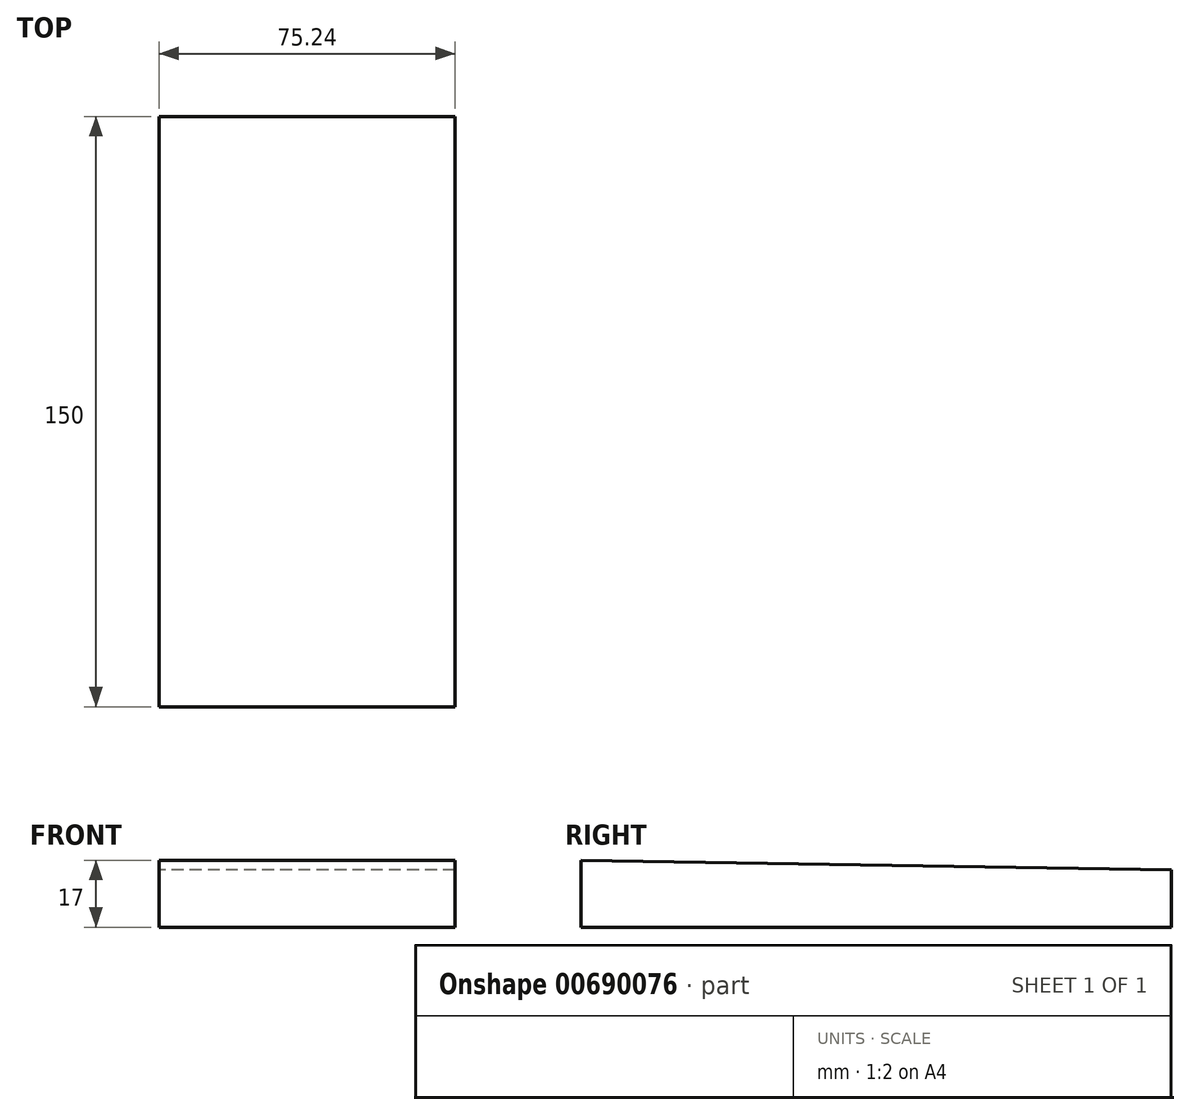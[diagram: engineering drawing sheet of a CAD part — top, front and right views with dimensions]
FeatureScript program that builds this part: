
annotation { "Feature Type Name" : "Feature", "Feature Type Description" : "" }
export const myFeature = defineFeature(function(context is Context, id is Id, definition is map)
    precondition{}
    {
        {
            var Q0;
            Q0=qCreatedBy(makeId("Front.planeOp"),FACE);
            var sketch = newSketch(context, id + "F0", { "sketchPlane" : qUnion([Q0])});
            skLineSegment(sketch, "E0.bottom", {"start": v(37.62, -8) * mm, "end": v(-37.62, -8) * mm});
            skLineSegment(sketch, "E0.top", {"start": v(37.62, 8) * mm, "end": v(-37.62, 8) * mm});
            skLineSegment(sketch, "E0.left", {"start": v(37.62, -8) * mm, "end": v(37.62, 8) * mm});
            skLineSegment(sketch, "E0.right", {"start": v(-37.62, -8) * mm, "end": v(-37.62, 8) * mm});
            skPoint(sketch, "E0.middle", {"position": v(0, 0) * mm});
            skSolve(sketch);
        }
        {
            var Q0;
            Q0=qCreatedBy(makeId("Right.planeOp"),FACE);
            var sketch = newSketch(context, id + "F1", { "sketchPlane" : qUnion([Q0])});
            skLineSegment(sketch, "E1.bottom", {"start": v(0, 8.5) * mm, "end": v(150, 6) * mm});
            skLineSegment(sketch, "E1.top", {"start": v(0, -8.5) * mm, "end": v(150, -8.5) * mm});
            skLineSegment(sketch, "E1.left", {"start": v(0, 8.5) * mm, "end": v(0, -8.5) * mm});
            skLineSegment(sketch, "E1.right", {"start": v(150, 6) * mm, "end": v(150, -8.5) * mm});
            skSolve(sketch);
        }
        {
            var Q0;
            Q0=makeQuery(id+"F1.imprint","IMPRINT",FACE,{"disambiguationData":[TD([[makeQuery(id+"F1.imprint","IMPRINT",EDGE,{"derivedFrom":sQuery(id+"F1.wireOp",EDGE,"E1.bottom")}),-1.0]])]});
            extrude(context, id + "F2", {"entities" : qUnion([Q0]), "depth" : 37.62 * mm, "offsetDistance" : 25 * mm});
        }
        {
            var Q0;
            Q0=makeQuery(id+"F2.opExtrude","CAP_FACE",FACE,{"disambiguationData":[OSD([sQuery(id+"F1.wireOp",EDGE,"E1.bottom"),sQuery(id+"F1.wireOp",EDGE,"E1.top"),sQuery(id+"F1.wireOp",EDGE,"E1.left"),sQuery(id+"F1.wireOp",EDGE,"E1.right")])],"isStart":true});
            extrude(context, id + "F3", {"entities" : qUnion([Q0]), "operationType" : NewBodyOperationType.ADD, "depth" : 37.62 * mm, "offsetDistance" : 25 * mm});
        }
    });
